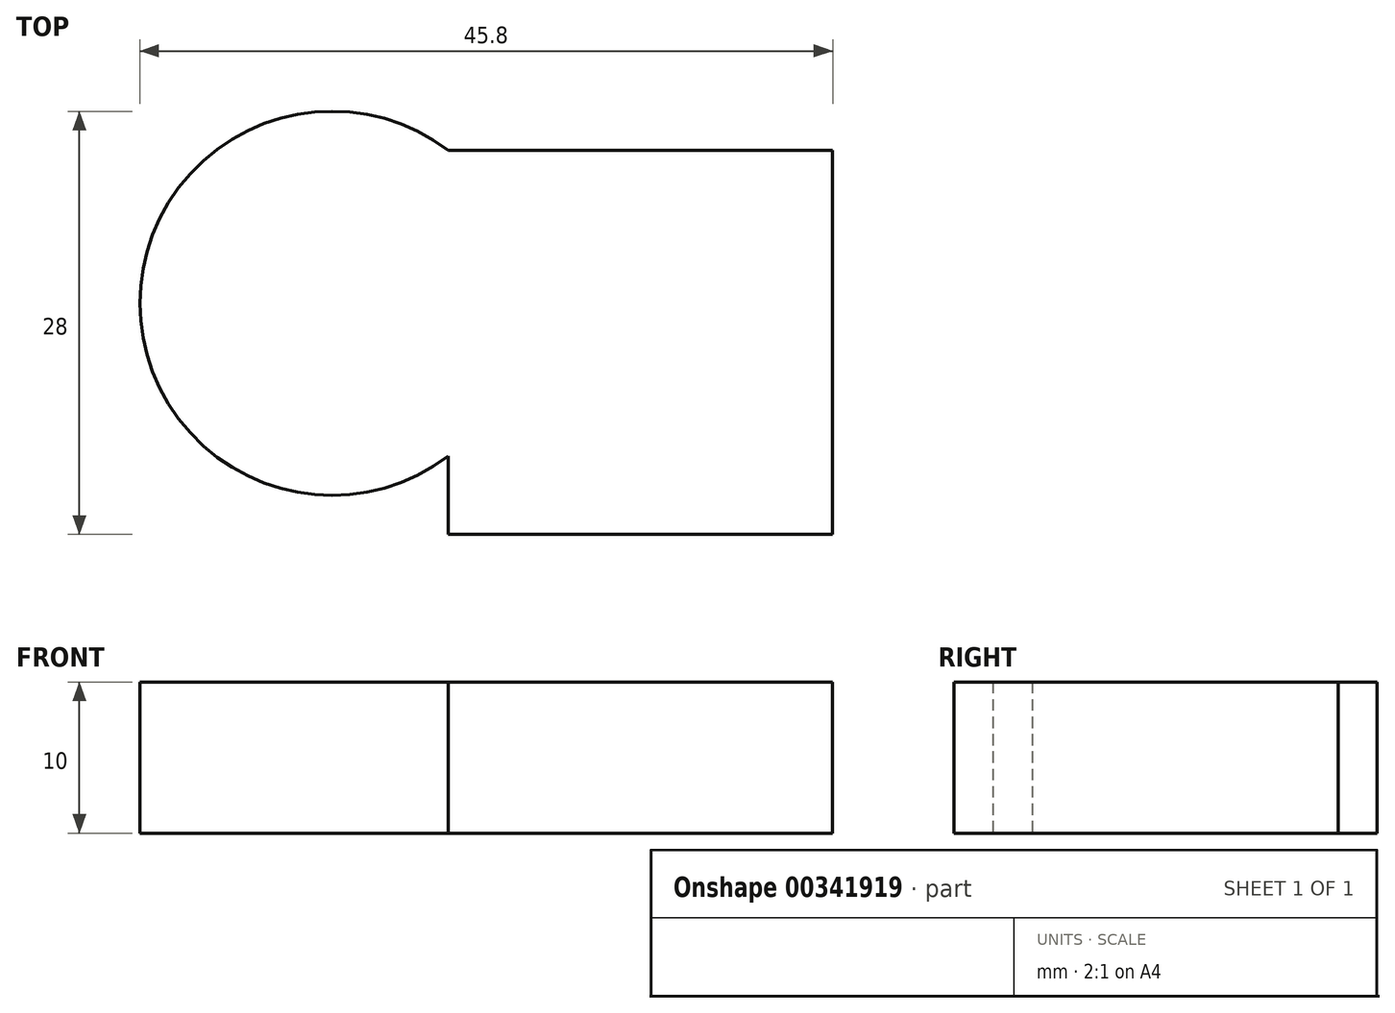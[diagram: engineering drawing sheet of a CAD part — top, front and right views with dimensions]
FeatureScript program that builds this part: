
annotation { "Feature Type Name" : "Feature", "Feature Type Description" : "" }
export const myFeature = defineFeature(function(context is Context, id is Id, definition is map)
    precondition{}
    {
        {
            var Q0;
            Q0=qCreatedBy(makeId("Top.planeOp"),FACE);
            var sketch = newSketch(context, id + "F0", { "sketchPlane" : qUnion([Q0])});
            skCircle(sketch, "E0", {"center": v(0, 0) * mm, "radius": 12.7 * mm});
            skLineSegment(sketch, "E1.bottom", {"start": v(7.7, 10.1) * mm, "end": v(33.1, 10.1) * mm});
            skLineSegment(sketch, "E1.top", {"start": v(7.7, -15.3) * mm, "end": v(33.1, -15.3) * mm});
            skLineSegment(sketch, "E1.left", {"start": v(7.7, 10.1) * mm, "end": v(7.7, -15.3) * mm});
            skLineSegment(sketch, "E1.right", {"start": v(33.1, 10.1) * mm, "end": v(33.1, -15.3) * mm});
            skSolve(sketch);
        }
        {
            var Q0;
            Q0 = qSketchRegion(id + "F0", true);
            extrude(context, id + "F1", {"entities" : qUnion([Q0]), "depth" : 10 * mm});
        }
    });
